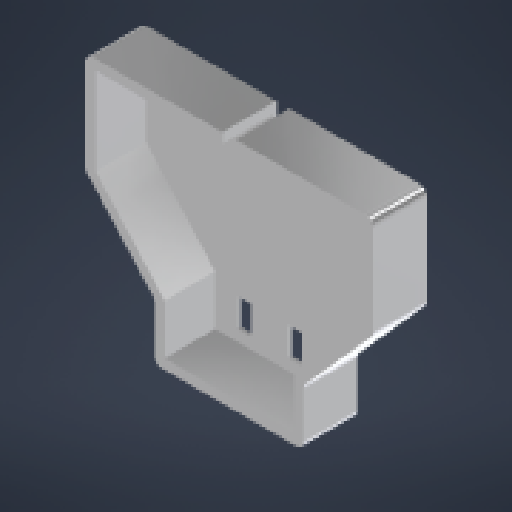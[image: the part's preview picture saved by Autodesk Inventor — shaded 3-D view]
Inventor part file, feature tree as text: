
AUTODESK INVENTOR PART (.ipt)
format: ipt  version: 2023 (Build 270158000, 158)  size: 207,360 bytes
history: native  units: in
note: dims shown in document units (in); Inventor stores cm internally (conversion verified against a paired STEP export)
features: extrude x4, reference x4, sketch x3, plane x1, fillet x1, other x1
ambient origin geometry x8: Origin, YZ Plane, XZ Plane, XY Plane, X Axis, Y Axis, Z Axis, Center Point
bodies: Solid1 (feature_tree)
feature tree (14):
  plane  "Work Plane1"
  sketch  "Sketch1"  dims[d1=1.6356in d2=0.778in]
  extrude  "Extrusion1"  Depth=0.778in
  extrude  "Extrusion2"  Depth=0.79in
  extrude  "Extrusion3"  Depth=0.02in
  fillet  "Fillet1"  Radius=1.315in
  extrude  "Extrusion4"  Depth=0.225in
  sketch  "Sketch2"  dims[d3=0.778in d6=0.79in]
  sketch  "Sketch4"  dims[d7=0.9503in d8=0.9503in d9=1.315in d10=0.225in d11=1.0087in d12=0.0625in d13=0.33in d14=0.0in d15=0.02in d16=0.0in d17=0.0in d18=0.0in d19=0.05in d30=0.3in d31=1.0in d32=0.0in d33=0.02in d34=0.02in d35=-0.2in]
  reference  "Reference1"
  reference  "Reference2"
  reference  "Reference3"
  reference  "Reference4"
  other  "kraken-power-adapter.iam"
